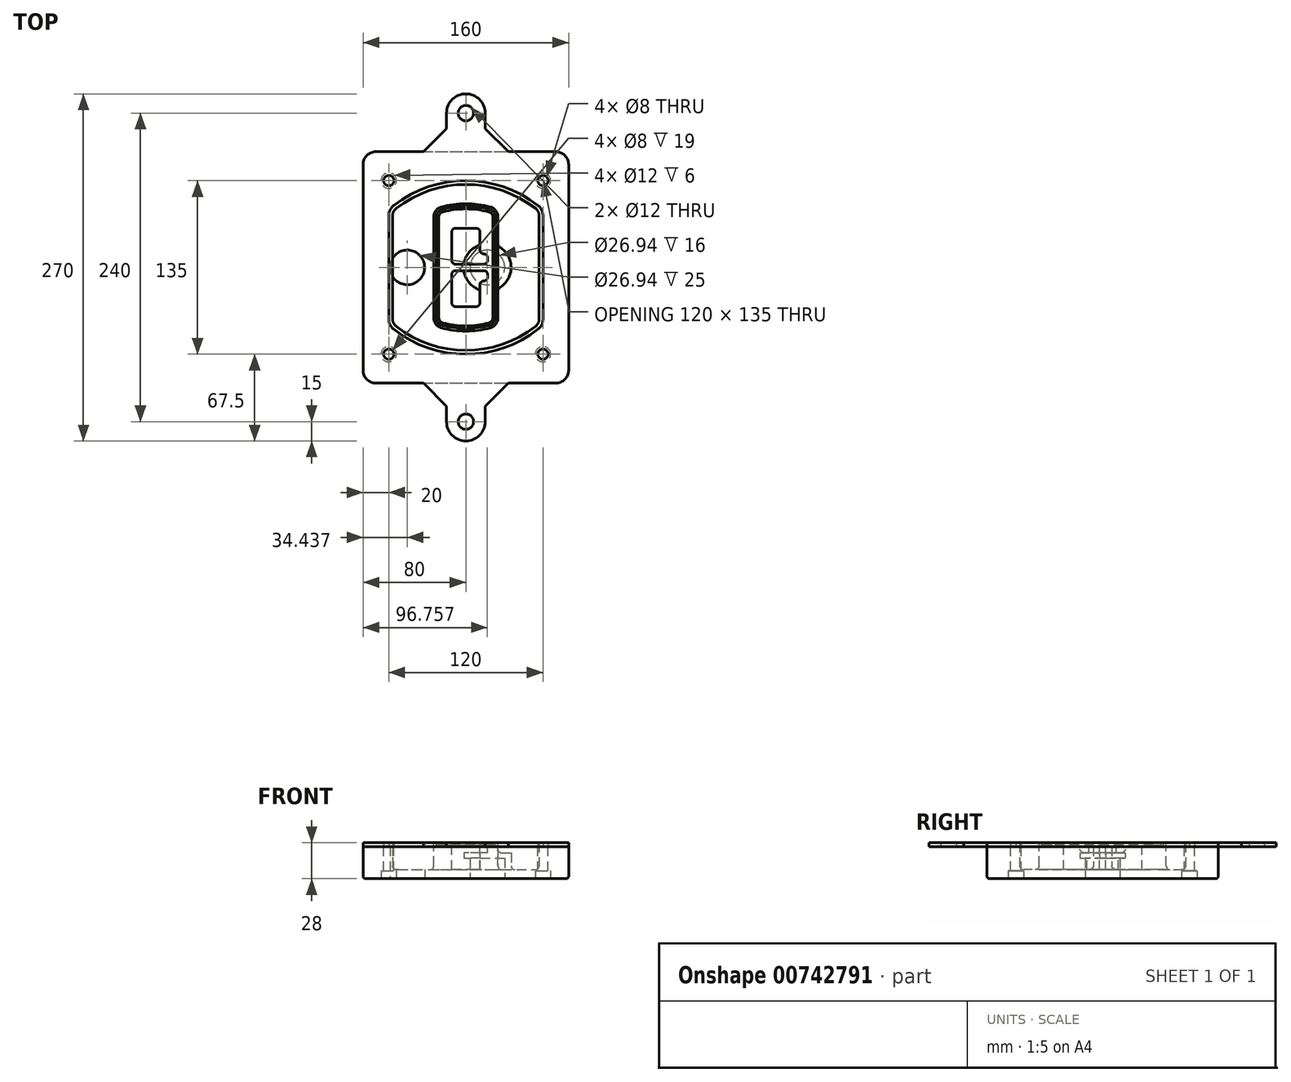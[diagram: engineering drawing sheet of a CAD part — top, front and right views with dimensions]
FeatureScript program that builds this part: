
annotation { "Feature Type Name" : "Feature", "Feature Type Description" : "" }
export const myFeature = defineFeature(function(context is Context, id is Id, definition is map)
    precondition{}
    {
        {
            var Q0;
            Q0=qCreatedBy(makeId("Top.planeOp"),FACE);
            var sketch = newSketch(context, id + "F0", { "sketchPlane" : qUnion([Q0])});
            skPoint(sketch, "E0.rect.middle", {"position": v(0, 0) * mm});
            skLineSegment(sketch, "E1.bottom", {"start": v(-70, -90) * mm, "end": v(70, -90) * mm});
            skLineSegment(sketch, "E1.top", {"start": v(-70, 90) * mm, "end": v(70, 90) * mm});
            skLineSegment(sketch, "E1.left", {"start": v(-80, -80) * mm, "end": v(-80, 80) * mm});
            skLineSegment(sketch, "E1.right", {"start": v(80, -80) * mm, "end": v(80, 80) * mm});
            skLineSegment(sketch, "E2", {"start": v(-80, 90) * mm, "end": v(80, -90) * mm, "construction": true});
            skLineSegment(sketch, "E3", {"start": v(80, 90) * mm, "end": v(-80, -90) * mm, "construction": true});
            skCircle(sketch, "E4", {"center": v(-60, 67.5) * mm, "radius": 4 * mm});
            skCircle(sketch, "E5", {"center": v(60, 67.5) * mm, "radius": 4 * mm});
            skCircle(sketch, "E6", {"center": v(60, -67.5) * mm, "radius": 4 * mm});
            skCircle(sketch, "E7", {"center": v(-60, -67.5) * mm, "radius": 4 * mm});
            skLineSegment(sketch, "E8", {"start": v(-60, 67.5) * mm, "end": v(60, 67.5) * mm, "construction": true});
            skLineSegment(sketch, "E9", {"start": v(60, 67.5) * mm, "end": v(60, -67.5) * mm, "construction": true});
            skLineSegment(sketch, "E10", {"start": v(60, -67.5) * mm, "end": v(-60, -67.5) * mm, "construction": true});
            skLineSegment(sketch, "E11", {"start": v(-60, -67.5) * mm, "end": v(-60, 67.5) * mm, "construction": true});
            skLineSegment(sketch, "E12", {"start": v(-60, 40.3) * mm, "end": v(-60, -40.3) * mm});
            skLineSegment(sketch, "E13", {"start": v(60, 40.3) * mm, "end": v(60, -40.3) * mm});
            skArc(sketch, "E14", {"start": v(56.15, 48.18) * mm, "mid": v(0, 67.5) * mm, "end": v(-56.15, 48.18) * mm});
            skArc(sketch, "E15", {"start": v(-56.15, -48.18) * mm, "mid": v(0, -67.5) * mm, "end": v(56.15, -48.18) * mm});
            skLineSegment(sketch, "E16", {"start": v(-60, 0) * mm, "end": v(60, 0) * mm, "construction": true});
            skPoint(sketch, "E17.visualSharp", {"position": v(-60, -45) * mm});
            skArc(sketch, "E17.filletArc", {"start": v(-60, -40.3) * mm, "mid": v(-58.99, -44.68) * mm, "end": v(-56.15, -48.18) * mm});
            skPoint(sketch, "E18.visualSharp", {"position": v(-60, 45) * mm});
            skArc(sketch, "E18.filletArc", {"start": v(-56.15, 48.18) * mm, "mid": v(-58.99, 44.68) * mm, "end": v(-60, 40.3) * mm});
            skPoint(sketch, "E19.visualSharp", {"position": v(60, 45) * mm});
            skArc(sketch, "E19.filletArc", {"start": v(60, 40.3) * mm, "mid": v(58.99, 44.68) * mm, "end": v(56.15, 48.18) * mm});
            skPoint(sketch, "E20.visualSharp", {"position": v(60, -45) * mm});
            skArc(sketch, "E20.filletArc", {"start": v(56.15, -48.18) * mm, "mid": v(58.99, -44.68) * mm, "end": v(60, -40.3) * mm});
            skPoint(sketch, "E21.visualSharp", {"position": v(-80, 90) * mm});
            skArc(sketch, "E21.filletArc", {"start": v(-70, 90) * mm, "mid": v(-77.07, 87.07) * mm, "end": v(-80, 80) * mm});
            skPoint(sketch, "E22.visualSharp", {"position": v(80, 90) * mm});
            skArc(sketch, "E22.filletArc", {"start": v(80, 80) * mm, "mid": v(77.07, 87.07) * mm, "end": v(70, 90) * mm});
            skPoint(sketch, "E23.visualSharp", {"position": v(80, -90) * mm});
            skArc(sketch, "E23.filletArc", {"start": v(70, -90) * mm, "mid": v(77.07, -87.07) * mm, "end": v(80, -80) * mm});
            skPoint(sketch, "E24.visualSharp", {"position": v(-80, -90) * mm});
            skArc(sketch, "E24.filletArc", {"start": v(-80, -80) * mm, "mid": v(-77.07, -87.07) * mm, "end": v(-70, -90) * mm});
            skArc(sketch, "E25.0", {"start": v(57, 40.3) * mm, "mid": v(56.3, 43.36) * mm, "end": v(54.3, 45.81) * mm});
            skLineSegment(sketch, "E25.1", {"start": v(57, 40.3) * mm, "end": v(57, -40.3) * mm});
            skArc(sketch, "E25.2", {"start": v(54.3, -45.81) * mm, "mid": v(56.3, -43.36) * mm, "end": v(57, -40.3) * mm});
            skArc(sketch, "E25.3", {"start": v(-54.3, -45.81) * mm, "mid": v(0, -64.5) * mm, "end": v(54.3, -45.81) * mm});
            skArc(sketch, "E25.4", {"start": v(-57, -40.3) * mm, "mid": v(-56.3, -43.36) * mm, "end": v(-54.3, -45.81) * mm});
            skArc(sketch, "E25.5", {"start": v(54.3, 45.81) * mm, "mid": v(0, 64.5) * mm, "end": v(-54.3, 45.81) * mm});
            skLineSegment(sketch, "E25.6", {"start": v(-57, 40.3) * mm, "end": v(-57, -40.3) * mm});
            skArc(sketch, "E25.7", {"start": v(-54.3, 45.81) * mm, "mid": v(-56.3, 43.36) * mm, "end": v(-57, 40.3) * mm});
            skArc(sketch, "E26.0", {"start": v(-58.62, 51.33) * mm, "mid": v(-62.58, 46.43) * mm, "end": v(-64, 40.3) * mm});
            skArc(sketch, "E26.1", {"start": v(58.62, 51.33) * mm, "mid": v(0, 71.5) * mm, "end": v(-58.62, 51.33) * mm});
            skArc(sketch, "E26.2", {"start": v(64, 40.3) * mm, "mid": v(62.58, 46.43) * mm, "end": v(58.62, 51.33) * mm});
            skLineSegment(sketch, "E26.3", {"start": v(64, 40.3) * mm, "end": v(64, -40.3) * mm});
            skArc(sketch, "E26.4", {"start": v(58.62, -51.33) * mm, "mid": v(62.58, -46.43) * mm, "end": v(64, -40.3) * mm});
            skLineSegment(sketch, "E26.5", {"start": v(-64, 40.3) * mm, "end": v(-64, -40.3) * mm});
            skArc(sketch, "E26.6", {"start": v(-58.62, -51.33) * mm, "mid": v(0, -71.5) * mm, "end": v(58.62, -51.33) * mm});
            skArc(sketch, "E26.7", {"start": v(-64, -40.3) * mm, "mid": v(-62.58, -46.43) * mm, "end": v(-58.62, -51.33) * mm});
            skSolve(sketch);
        }
        {
            var Q0;
            Q0=makeQuery(id+"F0.imprint","IMPRINT",FACE,{"disambiguationData":[TD([[makeQuery(id+"F0.imprint","IMPRINT",EDGE,{"derivedFrom":sQuery(id+"F0.wireOp",EDGE,"E1.bottom")}),1.0]])]});
            var Q1;
            Q1=makeQuery(id+"F0.imprint","IMPRINT",FACE,{"disambiguationData":[TD([[makeQuery(id+"F0.imprint","IMPRINT",EDGE,{"derivedFrom":sQuery(id+"F0.wireOp",EDGE,"E12")}),1.0]])]});
            var Q2;
            Q2=makeQuery(id+"F0.imprint","IMPRINT",FACE,{"disambiguationData":[TD([[makeQuery(id+"F0.imprint","IMPRINT",EDGE,{"derivedFrom":sQuery(id+"F0.wireOp",EDGE,"E25.0")}),1.0]])]});
            var Q3;
            Q3=makeQuery(id+"F0.imprint","IMPRINT",FACE,{"disambiguationData":[TD([[makeQuery(id+"F0.imprint","IMPRINT",EDGE,{"derivedFrom":sQuery(id+"F0.wireOp",EDGE,"E12")}),-1.0]])]});
            extrude(context, id + "F1", {"entities" : qUnion([Q0, Q1, Q2, Q3]), "oppositeDirection" : true, "depth" : 25 * mm});
        }
        {
            var Q0;
            Q0=makeQuery(id+"F0.imprint","IMPRINT",FACE,{"disambiguationData":[TD([[makeQuery(id+"F0.imprint","IMPRINT",EDGE,{"derivedFrom":sQuery(id+"F0.wireOp",EDGE,"E12")}),1.0]])]});
            extrude(context, id + "F2", {"entities" : qUnion([Q0]), "operationType" : NewBodyOperationType.ADD, "depth" : 3 * mm});
        }
        {
            var Q0;
            Q0=makeQuery(id+"F0.imprint","IMPRINT",FACE,{"disambiguationData":[TD([[makeQuery(id+"F0.imprint","IMPRINT",EDGE,{"derivedFrom":sQuery(id+"F0.wireOp",EDGE,"E25.0")}),1.0]])]});
            extrude(context, id + "F3", {"entities" : qUnion([Q0]), "operationType" : NewBodyOperationType.REMOVE, "oppositeDirection" : true, "depth" : 18 * mm});
        }
        {
            var Q0;
            Q0=makeQuery(id+"F2.opExtrude","CAP_FACE",FACE,{"disambiguationData":[OSD([sQuery(id+"F0.wireOp",EDGE,"E12"),sQuery(id+"F0.wireOp",EDGE,"E13"),sQuery(id+"F0.wireOp",EDGE,"E14"),sQuery(id+"F0.wireOp",EDGE,"E15"),sQuery(id+"F0.wireOp",EDGE,"E17.filletArc"),sQuery(id+"F0.wireOp",EDGE,"E18.filletArc"),sQuery(id+"F0.wireOp",EDGE,"E19.filletArc"),sQuery(id+"F0.wireOp",EDGE,"E20.filletArc"),sQuery(id+"F0.wireOp",EDGE,"E25.0"),sQuery(id+"F0.wireOp",EDGE,"E25.1"),sQuery(id+"F0.wireOp",EDGE,"E25.2"),sQuery(id+"F0.wireOp",EDGE,"E25.3"),sQuery(id+"F0.wireOp",EDGE,"E25.4"),sQuery(id+"F0.wireOp",EDGE,"E25.5"),sQuery(id+"F0.wireOp",EDGE,"E25.6"),sQuery(id+"F0.wireOp",EDGE,"E25.7")])],"isStart":false});
            var sketch = newSketch(context, id + "F4", { "sketchPlane" : qUnion([Q0])});
            skArc(sketch, "E27.0", {"start": v(-19.08, -46.97) * mm, "mid": v(0, -49.5) * mm, "end": v(19.08, -46.97) * mm});
            skArc(sketch, "E28.0", {"start": v(19.08, 46.97) * mm, "mid": v(0, 49.5) * mm, "end": v(-19.08, 46.97) * mm});
            skLineSegment(sketch, "E29", {"start": v(-25, 39.25) * mm, "end": v(-25, -39.25) * mm});
            skLineSegment(sketch, "E30", {"start": v(25, 39.25) * mm, "end": v(25, -39.25) * mm});
            skLineSegment(sketch, "E31", {"start": v(-25, 45.1) * mm, "end": v(25, 45.1) * mm, "construction": true});
            skLineSegment(sketch, "E32", {"start": v(-25, -45.1) * mm, "end": v(25, -45.1) * mm, "construction": true});
            skPoint(sketch, "E33.visualSharp", {"position": v(-25, 45.1) * mm});
            skArc(sketch, "E33.filletArc", {"start": v(-19.08, 46.97) * mm, "mid": v(-23.35, 44.11) * mm, "end": v(-25, 39.25) * mm});
            skPoint(sketch, "E34.visualSharp", {"position": v(25, 45.1) * mm});
            skArc(sketch, "E34.filletArc", {"start": v(25, 39.25) * mm, "mid": v(23.35, 44.11) * mm, "end": v(19.08, 46.97) * mm});
            skPoint(sketch, "E35.visualSharp", {"position": v(25, -45.1) * mm});
            skArc(sketch, "E35.filletArc", {"start": v(19.08, -46.97) * mm, "mid": v(23.35, -44.11) * mm, "end": v(25, -39.25) * mm});
            skPoint(sketch, "E36.visualSharp", {"position": v(-25, -45.1) * mm});
            skArc(sketch, "E36.filletArc", {"start": v(-25, -39.25) * mm, "mid": v(-23.35, -44.11) * mm, "end": v(-19.08, -46.97) * mm});
            skArc(sketch, "E37.0", {"start": v(54.3, 45.81) * mm, "mid": v(0, 64.5) * mm, "end": v(-54.3, 45.81) * mm});
            skArc(sketch, "E37.1", {"start": v(-54.3, 45.81) * mm, "mid": v(-56.3, 43.36) * mm, "end": v(-57, 40.3) * mm});
            skLineSegment(sketch, "E37.2", {"start": v(-57, 40.3) * mm, "end": v(-57, -40.3) * mm});
            skArc(sketch, "E37.3", {"start": v(-57, -40.3) * mm, "mid": v(-56.3, -43.36) * mm, "end": v(-54.3, -45.81) * mm});
            skArc(sketch, "E37.4", {"start": v(-54.3, -45.81) * mm, "mid": v(0, -64.5) * mm, "end": v(54.3, -45.81) * mm});
            skArc(sketch, "E37.5", {"start": v(54.3, -45.81) * mm, "mid": v(56.3, -43.36) * mm, "end": v(57, -40.3) * mm});
            skLineSegment(sketch, "E37.6", {"start": v(57, 40.3) * mm, "end": v(57, -40.3) * mm});
            skArc(sketch, "E37.7", {"start": v(57, 40.3) * mm, "mid": v(56.3, 43.36) * mm, "end": v(54.3, 45.81) * mm});
            skLineSegment(sketch, "E38.0", {"start": v(23, 39.25) * mm, "end": v(23, -39.25) * mm});
            skArc(sketch, "E38.1", {"start": v(18.56, -45.04) * mm, "mid": v(21.76, -42.9) * mm, "end": v(23, -39.25) * mm});
            skArc(sketch, "E38.2", {"start": v(-18.56, -45.04) * mm, "mid": v(0, -47.5) * mm, "end": v(18.56, -45.04) * mm});
            skArc(sketch, "E38.3", {"start": v(-23, -39.25) * mm, "mid": v(-21.76, -42.9) * mm, "end": v(-18.56, -45.04) * mm});
            skLineSegment(sketch, "E38.4", {"start": v(-23, 39.25) * mm, "end": v(-23, -39.25) * mm});
            skArc(sketch, "E38.5", {"start": v(23, 39.25) * mm, "mid": v(21.76, 42.9) * mm, "end": v(18.56, 45.04) * mm});
            skArc(sketch, "E38.6", {"start": v(-18.56, 45.04) * mm, "mid": v(-21.76, 42.9) * mm, "end": v(-23, 39.25) * mm});
            skArc(sketch, "E38.7", {"start": v(18.56, 45.04) * mm, "mid": v(0, 47.5) * mm, "end": v(-18.56, 45.04) * mm});
            skArc(sketch, "E39.0", {"start": v(21, 39.25) * mm, "mid": v(20.18, 41.68) * mm, "end": v(18.04, 43.1) * mm});
            skLineSegment(sketch, "E39.1", {"start": v(21, 39.25) * mm, "end": v(21, -39.25) * mm});
            skArc(sketch, "E39.2", {"start": v(18.04, -43.1) * mm, "mid": v(20.18, -41.68) * mm, "end": v(21, -39.25) * mm});
            skArc(sketch, "E39.3", {"start": v(-18.04, -43.1) * mm, "mid": v(0, -45.5) * mm, "end": v(18.04, -43.1) * mm});
            skArc(sketch, "E39.4", {"start": v(-21, -39.25) * mm, "mid": v(-20.18, -41.68) * mm, "end": v(-18.04, -43.1) * mm});
            skArc(sketch, "E39.5", {"start": v(18.04, 43.1) * mm, "mid": v(0, 45.5) * mm, "end": v(-18.04, 43.1) * mm});
            skLineSegment(sketch, "E39.6", {"start": v(-21, 39.25) * mm, "end": v(-21, -39.25) * mm});
            skArc(sketch, "E39.7", {"start": v(-18.04, 43.1) * mm, "mid": v(-20.18, 41.68) * mm, "end": v(-21, 39.25) * mm});
            skLineSegment(sketch, "E40", {"start": v(-25, 0) * mm, "end": v(25, 0) * mm, "construction": true});
            skLineSegment(sketch, "E41", {"start": v(-11, 5.5) * mm, "end": v(-11, 27.5) * mm});
            skLineSegment(sketch, "E42", {"start": v(-8, 30.5) * mm, "end": v(8, 30.5) * mm});
            skLineSegment(sketch, "E43", {"start": v(11, 27.5) * mm, "end": v(11, 13.5) * mm});
            skLineSegment(sketch, "E44", {"start": v(14, 10.5) * mm, "end": v(14, 10.5) * mm});
            skLineSegment(sketch, "E45", {"start": v(17, 7.5) * mm, "end": v(17, 5.5) * mm});
            skLineSegment(sketch, "E46", {"start": v(14, 2.5) * mm, "end": v(-8, 2.5) * mm});
            skPoint(sketch, "E47.visualSharp", {"position": v(-11, 30.5) * mm});
            skArc(sketch, "E47.filletArc", {"start": v(-8, 30.5) * mm, "mid": v(-10.12, 29.62) * mm, "end": v(-11, 27.5) * mm});
            skPoint(sketch, "E48.visualSharp", {"position": v(11, 30.5) * mm});
            skArc(sketch, "E48.filletArc", {"start": v(11, 27.5) * mm, "mid": v(10.12, 29.62) * mm, "end": v(8, 30.5) * mm});
            skPoint(sketch, "E49.visualSharp", {"position": v(11, 10.5) * mm});
            skArc(sketch, "E49.filletArc", {"start": v(11, 13.5) * mm, "mid": v(11.88, 11.38) * mm, "end": v(14, 10.5) * mm});
            skPoint(sketch, "E50.visualSharp", {"position": v(17, 10.5) * mm});
            skArc(sketch, "E50.filletArc", {"start": v(17, 7.5) * mm, "mid": v(16.12, 9.62) * mm, "end": v(14, 10.5) * mm});
            skPoint(sketch, "E51.visualSharp", {"position": v(17, 2.5) * mm});
            skArc(sketch, "E51.filletArc", {"start": v(14, 2.5) * mm, "mid": v(16.12, 3.38) * mm, "end": v(17, 5.5) * mm});
            skPoint(sketch, "E52.visualSharp", {"position": v(-11, 2.5) * mm});
            skArc(sketch, "E52.filletArc", {"start": v(-11, 5.5) * mm, "mid": v(-10.12, 3.38) * mm, "end": v(-8, 2.5) * mm});
            skLineSegment(sketch, "E53.0.MirrorCS", {"start": v(14, -2.5) * mm, "end": v(-8, -2.5) * mm});
            skArc(sketch, "E54.0.MirrorCS", {"start": v(-11, -5.5) * mm, "mid": v(-10.12, -3.38) * mm, "end": v(-8, -2.5) * mm});
            skLineSegment(sketch, "E55.0.MirrorCS", {"start": v(-11, -5.5) * mm, "end": v(-11, -27.5) * mm});
            skArc(sketch, "E56.0.MirrorCS", {"start": v(-8, -30.5) * mm, "mid": v(-10.12, -29.62) * mm, "end": v(-11, -27.5) * mm});
            skLineSegment(sketch, "E57.0.MirrorCS", {"start": v(-8, -30.5) * mm, "end": v(8, -30.5) * mm});
            skArc(sketch, "E58.0.MirrorCS", {"start": v(11, -27.5) * mm, "mid": v(10.12, -29.62) * mm, "end": v(8, -30.5) * mm});
            skLineSegment(sketch, "E59.0.MirrorCS", {"start": v(11, -27.5) * mm, "end": v(11, -13.5) * mm});
            skArc(sketch, "E60.0.MirrorCS", {"start": v(11, -13.5) * mm, "mid": v(11.88, -11.38) * mm, "end": v(14, -10.5) * mm});
            skArc(sketch, "E61.0.MirrorCS", {"start": v(17, -7.5) * mm, "mid": v(16.12, -9.62) * mm, "end": v(14, -10.5) * mm});
            skLineSegment(sketch, "E62.0.MirrorCS", {"start": v(17, -7.5) * mm, "end": v(17, -5.5) * mm});
            skArc(sketch, "E63.0.MirrorCS", {"start": v(14, -2.5) * mm, "mid": v(16.12, -3.38) * mm, "end": v(17, -5.5) * mm});
            skSolve(sketch);
        }
        {
            var Q0;
            Q0=makeQuery(id+"F4.imprint","IMPRINT",FACE,{"disambiguationData":[TD([[makeQuery(id+"F4.imprint","IMPRINT",EDGE,{"derivedFrom":sQuery(id+"F4.wireOp",EDGE,"E27.0")}),1.0]])]});
            var Q1;
            Q1=makeQuery(id+"F4.imprint","IMPRINT",FACE,{"disambiguationData":[TD([[makeQuery(id+"F4.imprint","IMPRINT",EDGE,{"derivedFrom":sQuery(id+"F4.wireOp",EDGE,"E38.0")}),-1.0]])]});
            var Q2;
            Q2=makeQuery(id+"F4.imprint","IMPRINT",FACE,{"disambiguationData":[TD([[makeQuery(id+"F4.imprint","IMPRINT",EDGE,{"derivedFrom":sQuery(id+"F4.wireOp",EDGE,"E39.0")}),1.0]])]});
            extrude(context, id + "F5", {"entities" : qUnion([Q0, Q1, Q2]), "operationType" : NewBodyOperationType.ADD, "endBound" : BoundingType.UP_TO_NEXT, "oppositeDirection" : true, "depth" : 25 * mm});
        }
        {
            var Q0;
            Q0=makeQuery(id+"F4.imprint","IMPRINT",FACE,{"disambiguationData":[TD([[makeQuery(id+"F4.imprint","IMPRINT",EDGE,{"derivedFrom":sQuery(id+"F4.wireOp",EDGE,"E38.0")}),-1.0]])]});
            extrude(context, id + "F6", {"entities" : qUnion([Q0]), "operationType" : NewBodyOperationType.REMOVE, "oppositeDirection" : true, "depth" : 2 * mm});
        }
        {
            var Q0;
            Q0=makeQuery(id+"F1.opExtrude","CAP_FACE",FACE,{"disambiguationData":[OSD([sQuery(id+"F0.wireOp",EDGE,"E1.bottom"),sQuery(id+"F0.wireOp",EDGE,"E1.top"),sQuery(id+"F0.wireOp",EDGE,"E1.left"),sQuery(id+"F0.wireOp",EDGE,"E1.right"),sQuery(id+"F0.wireOp",EDGE,"E4"),sQuery(id+"F0.wireOp",EDGE,"E5"),sQuery(id+"F0.wireOp",EDGE,"E6"),sQuery(id+"F0.wireOp",EDGE,"E7"),sQuery(id+"F0.wireOp",EDGE,"E21.filletArc"),sQuery(id+"F0.wireOp",EDGE,"E22.filletArc"),sQuery(id+"F0.wireOp",EDGE,"E23.filletArc"),sQuery(id+"F0.wireOp",EDGE,"E24.filletArc")])],"isStart":false});
            var sketch = newSketch(context, id + "F7", { "sketchPlane" : qUnion([Q0])});
            skCircle(sketch, "E64", {"center": v(16.76, 0) * mm, "radius": 13.47 * mm});
            skCircle(sketch, "E65", {"center": v(-45.56, 0) * mm, "radius": 13.47 * mm});
            skLineSegment(sketch, "E66", {"start": v(80, 0) * mm, "end": v(-80, 0) * mm});
            skCircle(sketch, "E67", {"center": v(16.76, 0) * mm, "radius": 18.47 * mm});
            skCircle(sketch, "E68", {"center": v(60, -67.5) * mm, "radius": 6 * mm});
            skCircle(sketch, "E69", {"center": v(-60, -67.5) * mm, "radius": 6 * mm});
            skCircle(sketch, "E70", {"center": v(-60, 67.5) * mm, "radius": 6 * mm});
            skCircle(sketch, "E71", {"center": v(60, 67.5) * mm, "radius": 6 * mm});
            skSolve(sketch);
        }
        {
            var Q0;
            {var subQ1=sQuery(id+"F7.wireOp",EDGE,"E66");var subQ4=sQuery(id+"F7.wireOp",EDGE,"E64");var subQ6=makeQuery(id+"F7.imprint","INTERSECT",VERTEX,{"disambiguationData":[OD(0.0)],"derivedFrom":[subQ4,subQ1]});Q0=makeQuery(id+"F7.imprint","IMPRINT",FACE,{"disambiguationData":[TD([[makeQuery(id+"F7.imprint","IMPRINT",EDGE,{"disambiguationData":[TD([[subQ6,-1.0]])],"derivedFrom":subQ4}),-1.0]])]});}
            var Q1;
            {var subQ0=sQuery(id+"F7.wireOp",EDGE,"E66");var subQ1=sQuery(id+"F7.wireOp",EDGE,"E64");var subQ3=makeQuery(id+"F7.imprint","INTERSECT",VERTEX,{"disambiguationData":[OD(0.0)],"derivedFrom":[subQ1,subQ0]});Q1=makeQuery(id+"F7.imprint","IMPRINT",FACE,{"disambiguationData":[TD([[makeQuery(id+"F7.imprint","IMPRINT",EDGE,{"disambiguationData":[TD([[subQ3,-1.0]])],"derivedFrom":subQ1}),1.0]])]});}
            var Q2;
            {var subQ0=sQuery(id+"F7.wireOp",EDGE,"E66");var subQ1=sQuery(id+"F7.wireOp",EDGE,"E64");var subQ3=makeQuery(id+"F7.imprint","INTERSECT",VERTEX,{"disambiguationData":[OD(0.0)],"derivedFrom":[subQ1,subQ0]});Q2=makeQuery(id+"F7.imprint","IMPRINT",FACE,{"disambiguationData":[TD([[makeQuery(id+"F7.imprint","IMPRINT",EDGE,{"disambiguationData":[TD([[subQ3,1.0]])],"derivedFrom":subQ1}),1.0]])]});}
            var Q3;
            {var subQ1=sQuery(id+"F7.wireOp",EDGE,"E66");var subQ4=sQuery(id+"F7.wireOp",EDGE,"E64");var subQ6=makeQuery(id+"F7.imprint","INTERSECT",VERTEX,{"disambiguationData":[OD(0.0)],"derivedFrom":[subQ4,subQ1]});Q3=makeQuery(id+"F7.imprint","IMPRINT",FACE,{"disambiguationData":[TD([[makeQuery(id+"F7.imprint","IMPRINT",EDGE,{"disambiguationData":[TD([[subQ6,1.0]])],"derivedFrom":subQ4}),-1.0]])]});}
            extrude(context, id + "F8", {"entities" : qUnion([Q0, Q1, Q2, Q3]), "operationType" : NewBodyOperationType.ADD, "oppositeDirection" : true, "depth" : 20 * mm});
        }
        {
            var Q0;
            {var subQ0=sQuery(id+"F7.wireOp",EDGE,"E66");var subQ1=sQuery(id+"F7.wireOp",EDGE,"E64");var subQ3=makeQuery(id+"F7.imprint","INTERSECT",VERTEX,{"disambiguationData":[OD(0.0)],"derivedFrom":[subQ1,subQ0]});Q0=makeQuery(id+"F7.imprint","IMPRINT",FACE,{"disambiguationData":[TD([[makeQuery(id+"F7.imprint","IMPRINT",EDGE,{"disambiguationData":[TD([[subQ3,-1.0]])],"derivedFrom":subQ1}),1.0]])]});}
            var Q1;
            {var subQ0=sQuery(id+"F7.wireOp",EDGE,"E66");var subQ1=sQuery(id+"F7.wireOp",EDGE,"E64");var subQ3=makeQuery(id+"F7.imprint","INTERSECT",VERTEX,{"disambiguationData":[OD(0.0)],"derivedFrom":[subQ1,subQ0]});Q1=makeQuery(id+"F7.imprint","IMPRINT",FACE,{"disambiguationData":[TD([[makeQuery(id+"F7.imprint","IMPRINT",EDGE,{"disambiguationData":[TD([[subQ3,1.0]])],"derivedFrom":subQ1}),1.0]])]});}
            extrude(context, id + "F9", {"entities" : qUnion([Q0, Q1]), "operationType" : NewBodyOperationType.REMOVE, "oppositeDirection" : true, "depth" : 16 * mm});
        }
        {
            var Q0;
            {var subQ0=sQuery(id+"F7.wireOp",EDGE,"E66");var subQ1=sQuery(id+"F7.wireOp",EDGE,"E65");var subQ3=makeQuery(id+"F7.imprint","INTERSECT",VERTEX,{"disambiguationData":[OD(0.0)],"derivedFrom":[subQ1,subQ0]});Q0=makeQuery(id+"F7.imprint","IMPRINT",FACE,{"disambiguationData":[TD([[makeQuery(id+"F7.imprint","IMPRINT",EDGE,{"disambiguationData":[TD([[subQ3,-1.0]])],"derivedFrom":subQ1}),1.0]])]});}
            var Q1;
            {var subQ0=sQuery(id+"F7.wireOp",EDGE,"E66");var subQ1=sQuery(id+"F7.wireOp",EDGE,"E65");var subQ3=makeQuery(id+"F7.imprint","INTERSECT",VERTEX,{"disambiguationData":[OD(0.0)],"derivedFrom":[subQ1,subQ0]});Q1=makeQuery(id+"F7.imprint","IMPRINT",FACE,{"disambiguationData":[TD([[makeQuery(id+"F7.imprint","IMPRINT",EDGE,{"disambiguationData":[TD([[subQ3,1.0]])],"derivedFrom":subQ1}),1.0]])]});}
            extrude(context, id + "F10", {"entities" : qUnion([Q0, Q1]), "operationType" : NewBodyOperationType.REMOVE, "oppositeDirection" : true, "depth" : 25 * mm});
        }
        {
            var Q0;
            Q0=makeQuery(id+"F7.imprint","IMPRINT",FACE,{"disambiguationData":[TD([[makeQuery(id+"F7.imprint","IMPRINT",EDGE,{"derivedFrom":sQuery(id+"F7.wireOp",EDGE,"E68")}),1.0]])]});
            var Q1;
            Q1=makeQuery(id+"F7.imprint","IMPRINT",FACE,{"disambiguationData":[TD([[makeQuery(id+"F7.imprint","IMPRINT",EDGE,{"derivedFrom":makeQuery(id+"F1.opExtrude","CAP_EDGE",EDGE,{"disambiguationData":[OSD([sQuery(id+"F0.wireOp",EDGE,"E5")])],"isStart":false})}),-1.0]])]});
            var Q2;
            Q2=makeQuery(id+"F7.imprint","IMPRINT",FACE,{"disambiguationData":[TD([[makeQuery(id+"F7.imprint","IMPRINT",EDGE,{"derivedFrom":sQuery(id+"F7.wireOp",EDGE,"E69")}),1.0]])]});
            var Q3;
            Q3=makeQuery(id+"F7.imprint","IMPRINT",FACE,{"disambiguationData":[TD([[makeQuery(id+"F7.imprint","IMPRINT",EDGE,{"derivedFrom":makeQuery(id+"F1.opExtrude","CAP_EDGE",EDGE,{"disambiguationData":[OSD([sQuery(id+"F0.wireOp",EDGE,"E4")])],"isStart":false})}),-1.0]])]});
            var Q4;
            Q4=makeQuery(id+"F7.imprint","IMPRINT",FACE,{"disambiguationData":[TD([[makeQuery(id+"F7.imprint","IMPRINT",EDGE,{"derivedFrom":sQuery(id+"F7.wireOp",EDGE,"E70")}),1.0]])]});
            var Q5;
            Q5=makeQuery(id+"F7.imprint","IMPRINT",FACE,{"disambiguationData":[TD([[makeQuery(id+"F7.imprint","IMPRINT",EDGE,{"derivedFrom":makeQuery(id+"F1.opExtrude","CAP_EDGE",EDGE,{"disambiguationData":[OSD([sQuery(id+"F0.wireOp",EDGE,"E7")])],"isStart":false})}),-1.0]])]});
            var Q6;
            Q6=makeQuery(id+"F7.imprint","IMPRINT",FACE,{"disambiguationData":[TD([[makeQuery(id+"F7.imprint","IMPRINT",EDGE,{"derivedFrom":sQuery(id+"F7.wireOp",EDGE,"E71")}),1.0]])]});
            var Q7;
            Q7=makeQuery(id+"F7.imprint","IMPRINT",FACE,{"disambiguationData":[TD([[makeQuery(id+"F7.imprint","IMPRINT",EDGE,{"derivedFrom":makeQuery(id+"F1.opExtrude","CAP_EDGE",EDGE,{"disambiguationData":[OSD([sQuery(id+"F0.wireOp",EDGE,"E6")])],"isStart":false})}),-1.0]])]});
            extrude(context, id + "F11", {"entities" : qUnion([Q0, Q1, Q2, Q3, Q4, Q5, Q6, Q7]), "operationType" : NewBodyOperationType.REMOVE, "oppositeDirection" : true, "depth" : 6 * mm});
        }
        {
            var Q0;
            Q0=makeQuery(id+"F9.boolean.opBoolean","COPY",FACE,{"derivedFrom":makeQuery(id+"F9.opExtrude","CAP_FACE",FACE,{"disambiguationData":[OSD([sQuery(id+"F7.wireOp",EDGE,"E64")])],"isStart":false})});
            var sketch = newSketch(context, id + "F12", { "sketchPlane" : qUnion([Q0])});
            skArc(sketch, "E72.0", {"start": v(11, 17.55) * mm, "mid": v(2.57, 11.82) * mm, "end": v(-1.54, 2.5) * mm});
            skArc(sketch, "E72.1", {"start": v(-1.54, -2.5) * mm, "mid": v(2.57, -11.82) * mm, "end": v(11, -17.55) * mm});
            skLineSegment(sketch, "E73", {"start": v(-1.54, -2.5) * mm, "end": v(14, -2.5) * mm});
            skLineSegment(sketch, "E74.0", {"start": v(14, 2.5) * mm, "end": v(-1.54, 2.5) * mm});
            skArc(sketch, "E74.1", {"start": v(14, 2.5) * mm, "mid": v(16.12, 3.38) * mm, "end": v(17, 5.5) * mm});
            skLineSegment(sketch, "E74.2", {"start": v(17, 7.5) * mm, "end": v(17, 5.5) * mm});
            skArc(sketch, "E74.3", {"start": v(17, 7.5) * mm, "mid": v(16.12, 9.62) * mm, "end": v(14, 10.5) * mm});
            skArc(sketch, "E74.4", {"start": v(11, 13.5) * mm, "mid": v(11.88, 11.38) * mm, "end": v(14, 10.5) * mm});
            skLineSegment(sketch, "E74.5", {"start": v(11, 17.55) * mm, "end": v(11, 13.5) * mm});
            skLineSegment(sketch, "E74.7", {"start": v(14, -2.5) * mm, "end": v(-1.54, -2.5) * mm});
            skArc(sketch, "E74.8", {"start": v(14, -2.5) * mm, "mid": v(16.12, -3.38) * mm, "end": v(17, -5.5) * mm});
            skLineSegment(sketch, "E74.9", {"start": v(17, -7.5) * mm, "end": v(17, -5.5) * mm});
            skArc(sketch, "E74.10", {"start": v(17, -7.5) * mm, "mid": v(16.12, -9.62) * mm, "end": v(14, -10.5) * mm});
            skArc(sketch, "E74.11", {"start": v(11, -13.5) * mm, "mid": v(11.88, -11.38) * mm, "end": v(14, -10.5) * mm});
            skLineSegment(sketch, "E74.12", {"start": v(11, -17.55) * mm, "end": v(11, -13.5) * mm});
            skPoint(sketch, "E75.orphan", {"position": v(11, -27.5) * mm});
            skPoint(sketch, "E76.orphan", {"position": v(-8, -2.5) * mm});
            skPoint(sketch, "E77.orphan", {"position": v(-8, 2.5) * mm});
            skPoint(sketch, "E78.orphan", {"position": v(11, 27.5) * mm});
            skSolve(sketch);
        }
        {
            var Q0;
            {var subQ7=sQuery(id+"F12.wireOp",EDGE,"E72.0");var subQ14=sQuery(id+"F12.wireOp",EDGE,"E72.1");var subQ16=sQuery(id+"F12.wireOp",EDGE,"E74.1");var subQ18=sQuery(id+"F12.wireOp",EDGE,"E74.8");Q0=qUnion([makeQuery(id+"F12.imprint","IMPRINT",FACE,{"disambiguationData":[TD([[makeQuery(id+"F12.imprint","IMPRINT",EDGE,{"derivedFrom":subQ7}),1.0]])]}),makeQuery(id+"F12.imprint","IMPRINT",FACE,{"disambiguationData":[TD([[makeQuery(id+"F12.imprint","IMPRINT",EDGE,{"derivedFrom":subQ14}),1.0]])]}),makeQuery(id+"F12.imprint","IMPRINT",FACE,{"disambiguationData":[TD([[makeQuery(id+"F12.imprint","IMPRINT",EDGE,{"derivedFrom":subQ16}),1.0]])]}),makeQuery(id+"F12.imprint","IMPRINT",FACE,{"disambiguationData":[TD([[makeQuery(id+"F12.imprint","IMPRINT",EDGE,{"derivedFrom":subQ18}),-1.0]])]})]);}
            var Q1;
            Q1=makeQuery(id+"F5.boolean.opBoolean","SPLIT",FACE,{"disambiguationData":[TD([makeQuery(id+"F5.opExtrude","SWEPT_FACE",FACE,{"disambiguationData":[OSD([sQuery(id+"F4.wireOp",EDGE,"E41")])]})])],"derivedFrom":makeQuery(id+"F3.boolean.opBoolean","COPY",FACE,{"derivedFrom":makeQuery(id+"F3.opExtrude","CAP_FACE",FACE,{"disambiguationData":[OSD([sQuery(id+"F0.wireOp",EDGE,"E25.0"),sQuery(id+"F0.wireOp",EDGE,"E25.1"),sQuery(id+"F0.wireOp",EDGE,"E25.2"),sQuery(id+"F0.wireOp",EDGE,"E25.3"),sQuery(id+"F0.wireOp",EDGE,"E25.4"),sQuery(id+"F0.wireOp",EDGE,"E25.5"),sQuery(id+"F0.wireOp",EDGE,"E25.6"),sQuery(id+"F0.wireOp",EDGE,"E25.7")])],"isStart":false})})});
            extrude(context, id + "F13", {"entities" : qUnion([Q0]), "operationType" : NewBodyOperationType.REMOVE, "endBound" : BoundingType.UP_TO_SURFACE, "endBoundEntityFace" : qUnion([Q1]), "depth" : 25 * mm});
        }
        {
            var Q0;
            Q0=makeQuery(id+"F3.boolean.opBoolean","COPY",EDGE,{"derivedFrom":makeQuery(id+"F3.opExtrude","CAP_EDGE",EDGE,{"disambiguationData":[OSD([sQuery(id+"F0.wireOp",EDGE,"E25.6")])],"isStart":false})});
            var Q1;
            Q1=makeQuery(id+"F8.boolean.opBoolean","INTERSECT",EDGE,{"derivedFrom":[makeQuery(id+"F5.opExtrude","SWEPT_FACE",FACE,{"disambiguationData":[OSD([sQuery(id+"F4.wireOp",EDGE,"E30")])]}),makeQuery(id+"F8.opExtrude","CAP_FACE",FACE,{"disambiguationData":[OSD([sQuery(id+"F7.wireOp",EDGE,"E67")])],"isStart":false})]});
            var Q2;
            Q2=makeQuery(id+"F8.boolean.opBoolean","INTERSECT",EDGE,{"disambiguationData":[OD(1.0)],"derivedFrom":[makeQuery(id+"F5.opExtrude","SWEPT_FACE",FACE,{"disambiguationData":[OSD([sQuery(id+"F4.wireOp",EDGE,"E30")])]}),makeQuery(id+"F8.opExtrude","SWEPT_FACE",FACE,{"disambiguationData":[OSD([sQuery(id+"F7.wireOp",EDGE,"E67")])]})]});
            var Q3;
            {var subQ0=sQuery(id+"F4.wireOp",EDGE,"E30");Q3=makeQuery(id+"F8.boolean.opBoolean","SPLIT",EDGE,{"disambiguationData":[TD([makeQuery(id+"F5.opExtrude","SWEPT_FACE",FACE,{"disambiguationData":[OSD([sQuery(id+"F4.wireOp",EDGE,"E35.filletArc")])]})])],"derivedFrom":makeQuery(id+"F5.opExtrude","CAP_EDGE",EDGE,{"disambiguationData":[OSD([subQ0])],"isStart":false})});}
            var Q4;
            {var subQ0=sQuery(id+"F0.wireOp",EDGE,"E25.7");var subQ1=sQuery(id+"F0.wireOp",EDGE,"E25.1");var subQ2=sQuery(id+"F0.wireOp",EDGE,"E25.6");var subQ3=sQuery(id+"F0.wireOp",EDGE,"E25.5");var subQ4=sQuery(id+"F0.wireOp",EDGE,"E25.4");var subQ5=sQuery(id+"F0.wireOp",EDGE,"E25.0");var subQ6=sQuery(id+"F0.wireOp",EDGE,"E25.2");var subQ7=sQuery(id+"F0.wireOp",EDGE,"E25.3");Q4=makeQuery(id+"F8.boolean.opBoolean","INTERSECT",EDGE,{"derivedFrom":[makeQuery(id+"F5.boolean.opBoolean","SPLIT",FACE,{"disambiguationData":[TD([makeQuery(id+"F2.opExtrude","SWEPT_FACE",FACE,{"disambiguationData":[OSD([subQ5])]})])],"derivedFrom":makeQuery(id+"F3.boolean.opBoolean","COPY",FACE,{"derivedFrom":makeQuery(id+"F3.opExtrude","CAP_FACE",FACE,{"disambiguationData":[OSD([subQ5,subQ1,subQ6,subQ7,subQ4,subQ3,subQ2,subQ0])],"isStart":false})})}),makeQuery(id+"F8.opExtrude","SWEPT_FACE",FACE,{"disambiguationData":[OSD([sQuery(id+"F7.wireOp",EDGE,"E67")])]})]});}
            var Q5;
            Q5=makeQuery(id+"F8.boolean.opBoolean","INTERSECT",EDGE,{"disambiguationData":[OD(0.0)],"derivedFrom":[makeQuery(id+"F5.opExtrude","SWEPT_FACE",FACE,{"disambiguationData":[OSD([sQuery(id+"F4.wireOp",EDGE,"E30")])]}),makeQuery(id+"F8.opExtrude","SWEPT_FACE",FACE,{"disambiguationData":[OSD([sQuery(id+"F7.wireOp",EDGE,"E67")])]})]});
            fillet(context, id + "F14", {"entities" : qUnion([Q0, Q1, Q2, Q3, Q4, Q5]), "radius" : 3 * mm, "tangentPropagation" : true, "allowEdgeOverflow" : false});
        }
        {
            var Q0;
            Q0=makeQuery(id+"F1.opExtrude","CAP_EDGE",EDGE,{"disambiguationData":[OSD([sQuery(id+"F0.wireOp",EDGE,"E1.bottom")])],"isStart":false});
            fillet(context, id + "F15", {"entities" : qUnion([Q0]), "radius" : 2 * mm, "tangentPropagation" : true, "allowEdgeOverflow" : false});
        }
        {
            var Q0;
            {var subQ0=sQuery(id+"F0.wireOp",EDGE,"E21.filletArc");var subQ1=sQuery(id+"F0.wireOp",EDGE,"E7");var subQ2=sQuery(id+"F0.wireOp",EDGE,"E6");var subQ3=sQuery(id+"F0.wireOp",EDGE,"E5");var subQ4=sQuery(id+"F0.wireOp",EDGE,"E4");var subQ5=sQuery(id+"F0.wireOp",EDGE,"E22.filletArc");var subQ6=sQuery(id+"F0.wireOp",EDGE,"E1.bottom");var subQ7=sQuery(id+"F0.wireOp",EDGE,"E1.right");var subQ8=sQuery(id+"F0.wireOp",EDGE,"E1.top");var subQ9=sQuery(id+"F0.wireOp",EDGE,"E1.left");var subQ10=sQuery(id+"F0.wireOp",EDGE,"E23.filletArc");var subQ11=sQuery(id+"F0.wireOp",EDGE,"E24.filletArc");Q0=makeQuery(id+"F2.boolean.opBoolean","SPLIT",FACE,{"disambiguationData":[TD([makeQuery(id+"F1.opExtrude","SWEPT_FACE",FACE,{"disambiguationData":[OSD([subQ6])]})])],"derivedFrom":makeQuery(id+"F1.opExtrude","CAP_FACE",FACE,{"disambiguationData":[OSD([subQ6,subQ8,subQ9,subQ7,subQ4,subQ3,subQ2,subQ1,subQ0,subQ5,subQ10,subQ11])],"isStart":true})});}
            var sketch = newSketch(context, id + "F16", { "sketchPlane" : qUnion([Q0])});
            skLineSegment(sketch, "E79", {"start": v(0, 90) * mm, "end": v(0, 120) * mm, "construction": true});
            skLineSegment(sketch, "E80", {"start": v(15, 120) * mm, "end": v(15, 108) * mm});
            skLineSegment(sketch, "E81", {"start": v(-15, 120) * mm, "end": v(-15, 108) * mm});
            skLineSegment(sketch, "E82", {"start": v(-15, 108) * mm, "end": v(-33, 90) * mm});
            skLineSegment(sketch, "E83", {"start": v(15, 108) * mm, "end": v(33, 90) * mm});
            skCircle(sketch, "E84", {"center": v(0, 120) * mm, "radius": 6 * mm});
            skArc(sketch, "E85", {"start": v(15, 120) * mm, "mid": v(0, 135) * mm, "end": v(-15, 120) * mm});
            skLineSegment(sketch, "E86", {"start": v(-80, 0) * mm, "end": v(80, 0) * mm, "construction": true});
            skArc(sketch, "E87.MirrorCS", {"start": v(15, -120) * mm, "mid": v(0, -135) * mm, "end": v(-15, -120) * mm});
            skCircle(sketch, "E88.MirrorC", {"center": v(0, -120) * mm, "radius": 6 * mm});
            skLineSegment(sketch, "E89.MirrorCS", {"start": v(0, -90) * mm, "end": v(0, -120) * mm, "construction": true});
            skLineSegment(sketch, "E90.MirrorCS", {"start": v(-15, -108) * mm, "end": v(-33, -90) * mm});
            skLineSegment(sketch, "E91.MirrorCS", {"start": v(-15, -120) * mm, "end": v(-15, -108) * mm});
            skLineSegment(sketch, "E92.MirrorCS", {"start": v(15, -120) * mm, "end": v(15, -108) * mm});
            skLineSegment(sketch, "E93.MirrorCS", {"start": v(15, -108) * mm, "end": v(33, -90) * mm});
            skSolve(sketch);
        }
        {
            var Q0;
            Q0=makeQuery(id+"F16.imprint","IMPRINT",FACE,{"disambiguationData":[TD([[makeQuery(id+"F16.imprint","IMPRINT",EDGE,{"derivedFrom":makeQuery(id+"F1.opExtrude","CAP_EDGE",EDGE,{"disambiguationData":[OSD([sQuery(id+"F0.wireOp",EDGE,"E1.left")])],"isStart":true})}),-1.0]])]});
            var Q1;
            Q1=makeQuery(id+"F16.imprint","IMPRINT",FACE,{"disambiguationData":[TD([[makeQuery(id+"F16.imprint","IMPRINT",EDGE,{"derivedFrom":sQuery(id+"F16.wireOp",EDGE,"E80")}),-1.0]])]});
            var Q2;
            Q2=makeQuery(id+"F16.imprint","IMPRINT",FACE,{"disambiguationData":[TD([[makeQuery(id+"F16.imprint","IMPRINT",EDGE,{"derivedFrom":sQuery(id+"F16.wireOp",EDGE,"E91.MirrorCS")}),-1.0]])]});
            var Q3;
            Q3=makeQuery(id+"F2.opExtrude","CAP_FACE",FACE,{"disambiguationData":[OSD([sQuery(id+"F0.wireOp",EDGE,"E12"),sQuery(id+"F0.wireOp",EDGE,"E13"),sQuery(id+"F0.wireOp",EDGE,"E14"),sQuery(id+"F0.wireOp",EDGE,"E15"),sQuery(id+"F0.wireOp",EDGE,"E17.filletArc"),sQuery(id+"F0.wireOp",EDGE,"E18.filletArc"),sQuery(id+"F0.wireOp",EDGE,"E19.filletArc"),sQuery(id+"F0.wireOp",EDGE,"E20.filletArc"),sQuery(id+"F0.wireOp",EDGE,"E25.0"),sQuery(id+"F0.wireOp",EDGE,"E25.1"),sQuery(id+"F0.wireOp",EDGE,"E25.2"),sQuery(id+"F0.wireOp",EDGE,"E25.3"),sQuery(id+"F0.wireOp",EDGE,"E25.4"),sQuery(id+"F0.wireOp",EDGE,"E25.5"),sQuery(id+"F0.wireOp",EDGE,"E25.6"),sQuery(id+"F0.wireOp",EDGE,"E25.7")])],"isStart":false});
            extrude(context, id + "F17", {"entities" : qUnion([Q0, Q1, Q2]), "endBound" : BoundingType.UP_TO_SURFACE, "depth" : 25 * mm, "endBoundEntityFace" : qUnion([Q3]), "offsetDistance" : 25 * mm});
        }
    });
